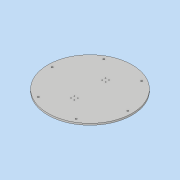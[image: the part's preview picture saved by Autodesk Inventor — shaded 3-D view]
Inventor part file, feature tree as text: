
AUTODESK INVENTOR PART (.ipt)
format: ipt  version: 2019 (Build 230136000, 136)  size: 161,792 bytes
history: native  units: mm
features: extrude x4, sketch x4, other x3, hole x3
ambient origin geometry x8: Origin, YZ Plane, XZ Plane, XY Plane, X Axis, Y Axis, Z Axis, Center Point
bodies: Body1 (feature_tree)
feature tree (14):
  other  "крепление2"
  other  "Твердое тело1"
  extrude  "Выдавливание8"  Depth=4.0mm
  hole  "Отверстие2"  [1 undecoded]
  hole  "Отверстие3"  [1 undecoded]
  extrude  "Выдавливание1"  Depth=4.0mm
  extrude  "Выдавливание4"  Depth=95.0mm
  extrude  "Выдавливание5"  Depth=4.0mm
  hole  "Отверстие1"  [1 undecoded]
  sketch  "Эскиз6"
  sketch  "Эскиз7"
  other  "Твердое тело2"
  sketch  "Эскиз8"
  sketch  "Эскиз9"
note: 3 required parameter values undecoded (feature->parameter linkage not recoverable at this tier; creation-order binding heuristic only, values carry confidence <= 0.55)
